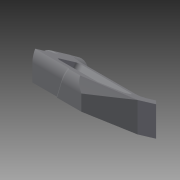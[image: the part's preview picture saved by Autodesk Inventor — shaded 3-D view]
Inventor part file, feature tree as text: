
AUTODESK INVENTOR PART (.ipt)
format: ipt  version: 2014 SP1 (Build 180222100, 222)  size: 508,416 bytes
history: native  units: in
note: dims shown in document units (in); Inventor stores cm internally (conversion verified against a paired STEP export)
features: sketch x25, projected_geometry x19, extrude x16, plane x6, fillet x4, revolve x3, sweep x2, chamfer x1, reference x1, other x1
ambient origin geometry x8: Origin, YZ Plane, XZ Plane, XY Plane, X Axis, Y Axis, Z Axis, Center Point
bodies: Solid1 (feature_tree)
feature tree (78):
  plane  "Work Plane1"
  extrude  "Extrusion1"  Depth=0.165in
  sketch  "Sketch2"  dims[d3=0.118in d4=0.1685in]
  plane  "Work Plane2"
  extrude  "Extrusion2"  Depth=0.1685in
  plane  "Work Plane3"
  extrude  "Extrusion3"  Depth=0.181in TaperAngle=0.0deg
  extrude  "Extrusion4"  Depth=0.181in TaperAngle=0.0deg
  sketch  "Sketch5"  dims[d13=0.02in d14=0.25in]
  sketch  "Sketch6"  dims[d15=0.19in d16=0.181in d17=0.0in]
  sketch  "Sketch7"  dims[d18=0.02in d19=0.125in d20=45.0deg d21=0.181in d22=0.0in]
  plane  "Work Plane4"
  extrude  "Extrusion5"  Depth=0.25in
  chamfer  "Chamfer1"  Distance=0.181in
  extrude  "Extrusion6"  Depth=0.181in TaperAngle=0.0deg
  sketch  "Sketch9"  dims[d26=0.9666in d27=0.9666in]
  plane  "Work Plane5"
  extrude  "Extrusion7"  Depth=0.181in TaperAngle=0.0deg
  sweep  "Sweep1"
  extrude  "Extrusion9"  Depth=0.0255in
  extrude  "Extrusion10"  Depth=0.102in
  plane  "Work Plane6"
  revolve  "Revolution1"  [1 undecoded]
  extrude  "Extrusion11"  TaperAngle=0.0deg  [1 undecoded]
  extrude  "Extrusion12"  Depth=0.0885in
  fillet  "Fillet3"  Radius=0.044in
  revolve  "Revolution2"  [1 undecoded]
  extrude  "Extrusion13"  Depth=0.044in
  sweep  "Sweep2"
  extrude  "Extrusion14"  Depth=0.056in TaperAngle=0.0deg
  extrude  "Extrusion15"  TaperAngle=90.0deg  [1 undecoded]
  fillet  "Fillet4"  Radius=0.056in
  fillet  "Fillet5"  [1 undecoded]
  fillet  "Fillet6"  Radius=0.056in
  extrude  "Extrusion16"  Depth=0.002in
  revolve  "Revolution3"  [1 undecoded]
  extrude  "Extrusion8"  Depth=0.0335in
  sketch  "Sketch1"  dims[d0=0.1185in d1=0.0in d2=0.165in]
  reference  "Reference1"
  sketch  "Sketch3"  dims[d5=0.1185in d6=0.0in d7=0.181in d8=0.0in]
  sketch  "Sketch4"  dims[d9=0.028in d11=0.181in d12=0.0in]
  projected_geometry  "Projected Loop1"
  projected_geometry  "Projected Loop2"
  projected_geometry  "Projected Loop3"
  projected_geometry  "Projected Loop4"
  sketch  "Sketch8"  dims[d23=0.083in d24=0.181in d25=0.0in]
  projected_geometry  "Projected Loop5"
  sketch  "Sketch10"  dims[d28=0.0in d29=0.0255in]
  projected_geometry  "Projected Loop6"
  sketch  "3D Sketch1"
  sketch  "Sketch11"  dims[d30=0.047in d31=0.102in]
  projected_geometry  "Projected Loop7"
  sketch  "Sketch12"  dims[d32=0.181in d33=0.0in d36=0.115in d37=0.0in]
  projected_geometry  "Projected Loop8"
  sketch  "Sketch13"  dims[d38=0.181in d39=0.0in d40=0.0in]
  other  "Work Axis1"
  sketch  "Sketch14"  dims[d41=90.0deg d43=0.0885in d48=0.044in]
  sketch  "Sketch15"  dims[d49=0.061in d50=0.089in]
  projected_geometry  "Projected Loop9"
  sketch  "Sketch16"  dims[d51=0.056in d52=0.0in d53=0.044in]
  projected_geometry  "Projected Loop10"
  sketch  "Sketch17"  dims[d54=0.087in d55=0.085in]
  sketch  "Sketch18"  dims[d56=0.0585in d57=0.056in d58=0.0in]
  projected_geometry  "Projected Loop11"
  sketch  "Sketch19"  dims[d59=0.03in d60=90.0deg d61=0.056in d62=0.0in d63=0.0in d64=0.056in d65=0.0in]
  projected_geometry  "Projected Loop12"
  sketch  "3D Sketch2"
  sketch  "Sketch20"  dims[d66=0.056in d67=0.0in d68=0.002in]
  projected_geometry  "Projected Loop13"
  sketch  "Sketch21"  dims[d69=0.03in d70=0.02in]
  projected_geometry  "Projected Loop14"
  sketch  "Sketch22"  dims[d71=0.014in d72=0.0335in]
  projected_geometry  "Projected Loop15"
  sketch  "Sketch23"  dims[d73=0.056in d74=0.0in d75=90.0deg]
  projected_geometry  "Projected Loop16"
  projected_geometry  "Project Cut Edges1"
  projected_geometry  "Project Cut Edges2"
  projected_geometry  "Project Cut Edges3"
note: 6 required parameter values undecoded (feature->parameter linkage not recoverable at this tier; creation-order binding heuristic only, values carry confidence <= 0.55)